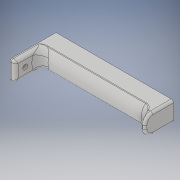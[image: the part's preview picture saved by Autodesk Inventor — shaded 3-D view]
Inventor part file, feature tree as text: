
AUTODESK INVENTOR PART (.ipt)
format: ipt  version: 2018 (Build 220112000, 112)  size: 366,080 bytes
history: native  units: in
note: dims shown in document units (in); Inventor stores cm internally (conversion verified against a paired STEP export)
features: extrude x7, sketch x7, projected_geometry x7, fillet x6, chamfer x1
ambient origin geometry x8: Origin, YZ Plane, XZ Plane, XY Plane, X Axis, Y Axis, Z Axis, Center Point
bodies: Solid1 (feature_tree)
feature tree (28):
  extrude  "Extrusion1"  Depth=0.5512in
  extrude  "Extrusion2"  Depth=3.7402in TaperAngle=0.0deg
  fillet  "Fillet3"  Radius=1.5748in
  fillet  "Fillet4"  Radius=0.1575in
  extrude  "Extrusion3"  Depth=0.2756in
  extrude  "Extrusion4"  Depth=0.1575in TaperAngle=0.0deg
  fillet  "Fillet5"  Radius=0.9843in
  fillet  "Fillet6"  Radius=0.1181in
  fillet  "Fillet7"  Radius=0.2756in
  extrude  "Extrusion5"  Depth=0.0394in
  chamfer  "Chamfer1"  Distance=0.1181in
  extrude  "Extrusion6"  Depth=0.0787in TaperAngle=45.0deg
  extrude  "Extrusion7"  Depth=0.1969in
  fillet  "Fillet8"  Radius=0.5512in
  sketch  "Sketch1"  dims[d1=0.6693in d2=0.5512in]
  sketch  "Sketch2"  dims[d3=0.4331in d4=3.7402in d5=0.0in d6=1.5748in d7=0.1575in d8=0.0in]
  sketch  "Sketch3"  dims[d11=0.1181in d12=0.2756in]
  sketch  "Sketch4"  dims[d13=0.1654in d14=0.1575in d15=0.0in d16=0.9843in d17=0.1181in d18=0.0in d19=0.2756in]
  sketch  "Sketch5"  dims[d20=0.0787in d21=0.0394in]
  sketch  "Sketch6"  dims[d22=0.1969in]
  projected_geometry  "Projected Loop1"
  projected_geometry  "Projected Loop2"
  projected_geometry  "Projected Loop3"
  projected_geometry  "Projected Loop4"
  projected_geometry  "Projected Loop5"
  projected_geometry  "Projected Loop6"
  sketch  "Sketch7"  dims[d23=0.3937in d24=0.1181in d25=0.0in d26=0.0787in d27=0.0787in d28=45.0deg d29=0.1969in d31=0.5512in d32=0.4331in d33=3.7402in d34=0.0in d35=0.1181in d36=0.0in d37=0.0787in]
  projected_geometry  "Projected Loop7"
